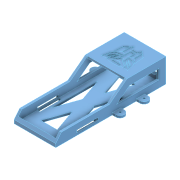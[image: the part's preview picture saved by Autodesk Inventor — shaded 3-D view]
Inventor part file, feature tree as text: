
AUTODESK INVENTOR PART (.ipt)
format: ipt  version: 2022 (Build 260153000, 153)  size: 468,480 bytes
history: native  units: mm
features: sketch x13, extrude x11, projected_geometry x10, fillet x2, rib x1, mirror x1, chamfer x1, hole x1
ambient origin geometry x8: Origin, YZ Plane, XZ Plane, XY Plane, X Axis, Y Axis, Z Axis, Center Point
bodies: Body1 (feature_tree)
feature tree (40):
  extrude  "Extrusion3"  Depth=143.0mm
  extrude  "Extrusion4"  Depth=3.0mm TaperAngle=0.0deg
  extrude  "Extrusion5"  Depth=3.0mm
  extrude  "Extrusion6"  Depth=5.0mm
  extrude  "Velcro Strap Hole"  Depth=5.0mm TaperAngle=0.0deg
  rib  "Rib1"
  mirror  "Mirror2"
  extrude  "Extrusion13"  Depth=5.0mm
  chamfer  "Chamfer4"  Distance=10.0mm
  extrude  "Extrusion8"  Depth=1.0mm
  extrude  "Extrusion9"  Depth=8.0mm TaperAngle=45.0deg
  hole  "Mounting Holes"  [1 undecoded]
  fillet  "Fillet1"  Radius=6.0mm
  extrude  "Extrusion10"  Depth=5.0mm
  extrude  "Autobots Logo"  Depth=30.0mm
  extrude  "Velcro Strap Hole 2"  Depth=34.0mm
  fillet  "Fillet2"  Radius=5.0mm
  sketch  "Sketch4"  dims[d25=51.0mm d26=143.0mm]
  sketch  "Sketch5"  dims[d27=4.0mm d28=3.0mm d29=0.0mm]
  sketch  "Sketch6"  dims[d30=3.0mm d31=3.0mm]
  sketch  "Sketch7"  dims[d33=50.0mm d34=0.0mm d36=5.0mm]
  sketch  "Sketch8"  dims[d37=3.0mm d38=5.0mm d39=0.0mm]
  sketch  "Sketch9"  dims[d40=15.0mm d41=5.0mm]
  sketch  "Sketch10"  dims[d42=0.0mm]
  sketch  "Sketch11"  dims[d43=30.0mm]
  sketch  "Sketch12"  dims[d45=4.0mm]
  sketch  "Sketch13"  dims[d46=45.0mm d47=10.0mm d48=0.0mm]
  sketch  "Sketch14"  dims[d49=25.0mm d50=1.0mm]
  sketch  "Sketch15"  dims[d51=3.0mm d52=0.0mm d53=0.0mm d54=1.0mm d55=1.0mm d56=8.0mm d57=10.0mm d58=45.0deg]
  sketch  "Sketch16"  dims[d59=10.0mm d60=10.0mm d61=0.0mm d62=6.0mm d64=5.0mm d65=30.0mm d66=34.0mm d67=5.0mm d68=6.0mm d69=10.0mm d70=0.0mm d71=3.4mm d72=6.0mm d73=4.0mm d74=2.0mm d75=90.0deg d76=6.0mm d77=0.0mm d78=5.0mm d81=20.0mm d82=10.0mm d83=15.0mm d84=10.0mm d85=0.0mm d86=1.0mm d87=0.0mm d88=28.0mm d89=3.0mm d90=3.0mm d91=10.0mm d92=0.0mm d93=3.0mm d94=3.0mm d95=10.0mm d96=0.0mm d97=1.0mm]
  projected_geometry  "Project Cut Edges2"
  projected_geometry  "Project Cut Edges3"
  projected_geometry  "Project Cut Edges4"
  projected_geometry  "Project Cut Edges5"
  projected_geometry  "Project Cut Edges6"
  projected_geometry  "Project Cut Edges7"
  projected_geometry  "Project Cut Edges8"
  projected_geometry  "Project Cut Edges9"
  projected_geometry  "Project Cut Edges10"
  projected_geometry  "Project Cut Edges11"
note: 1 required parameter value undecoded (feature->parameter linkage not recoverable at this tier; creation-order binding heuristic only, values carry confidence <= 0.55)
